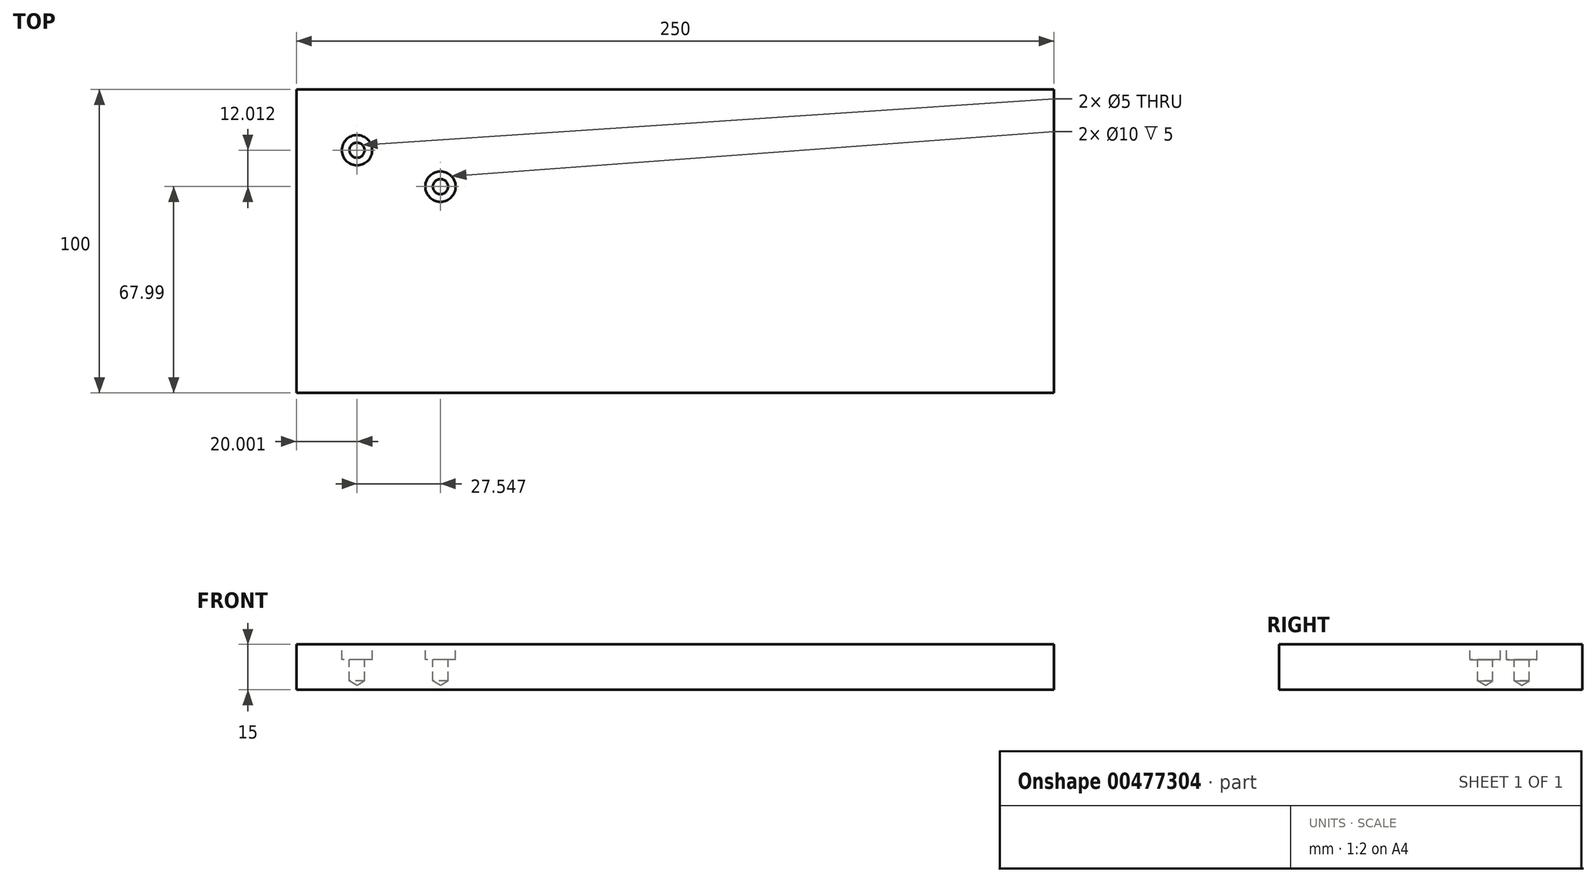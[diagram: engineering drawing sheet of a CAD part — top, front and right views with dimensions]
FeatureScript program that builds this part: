
annotation { "Feature Type Name" : "Feature", "Feature Type Description" : "" }
export const myFeature = defineFeature(function(context is Context, id is Id, definition is map)
    precondition{}
    {
        {
            var Q0;
            Q0=qCreatedBy(makeId("Top.planeOp"),FACE);
            var sketch = newSketch(context, id + "F0", { "sketchPlane" : qUnion([Q0])});
            skLineSegment(sketch, "E0.bottom", {"start": v(-123.53, 51.82) * mm, "end": v(126.47, 51.82) * mm});
            skLineSegment(sketch, "E0.top", {"start": v(-123.53, -48.18) * mm, "end": v(126.47, -48.18) * mm});
            skLineSegment(sketch, "E0.left", {"start": v(-123.53, 51.82) * mm, "end": v(-123.53, -48.18) * mm});
            skLineSegment(sketch, "E0.right", {"start": v(126.47, 51.82) * mm, "end": v(126.47, -48.18) * mm});
            skSolve(sketch);
        }
        {
            var Q0;
            Q0=makeQuery(id+"F0.imprint","IMPRINT",FACE,{"disambiguationData":[TD([[makeQuery(id+"F0.imprint","IMPRINT",EDGE,{"derivedFrom":sQuery(id+"F0.wireOp",EDGE,"E0.bottom")}),-1.0]])]});
            extrude(context, id + "F1", {"entities" : qUnion([Q0]), "depth" : 15 * mm});
        }
        {
            var Q0;
            Q0=makeQuery(id+"F1.opExtrude","CAP_FACE",FACE,{"disambiguationData":[OSD([sQuery(id+"F0.wireOp",EDGE,"E0.bottom"),sQuery(id+"F0.wireOp",EDGE,"E0.top"),sQuery(id+"F0.wireOp",EDGE,"E0.left"),sQuery(id+"F0.wireOp",EDGE,"E0.right")])],"isStart":false});
            var sketch = newSketch(context, id + "F2", { "sketchPlane" : qUnion([Q0])});
            skPoint(sketch, "E1", {"position": v(-75.98, 19.8) * mm});
            skPoint(sketch, "E2", {"position": v(-103.53, 31.82) * mm});
            skSolve(sketch);
        }
        {
            var Q0;
            Q0=sQuery(id+"F2.wireOp",VERTEX,"E2");
            var Q1;
            Q1=sQuery(id+"F2.wireOp",VERTEX,"E1");
            var Q2;
            Q2=makeQuery(id+"F1.opExtrude","SWEPT_BODY",BODY,{"disambiguationData":[OSD([sQuery(id+"F0.wireOp",EDGE,"E0.bottom"),sQuery(id+"F0.wireOp",EDGE,"E0.top"),sQuery(id+"F0.wireOp",EDGE,"E0.left"),sQuery(id+"F0.wireOp",EDGE,"E0.right")])]});
            hole(context, id + "F3", {"style" : HoleStyle.C_BORE, "endStyle" : HoleEndStyle.BLIND, "holeDiameter" : 5 * mm, "cBoreDiameter" : 10 * mm, "cBoreDepth" : 5 * mm, "holeDepth" : 12 * mm, "isTappedThrough" : true, "tappedDepth" : 12 * mm, "tapClearance" : 3, "locations" : qUnion([Q0, Q1]), "scope" : qUnion([Q2])});
        }
    });
